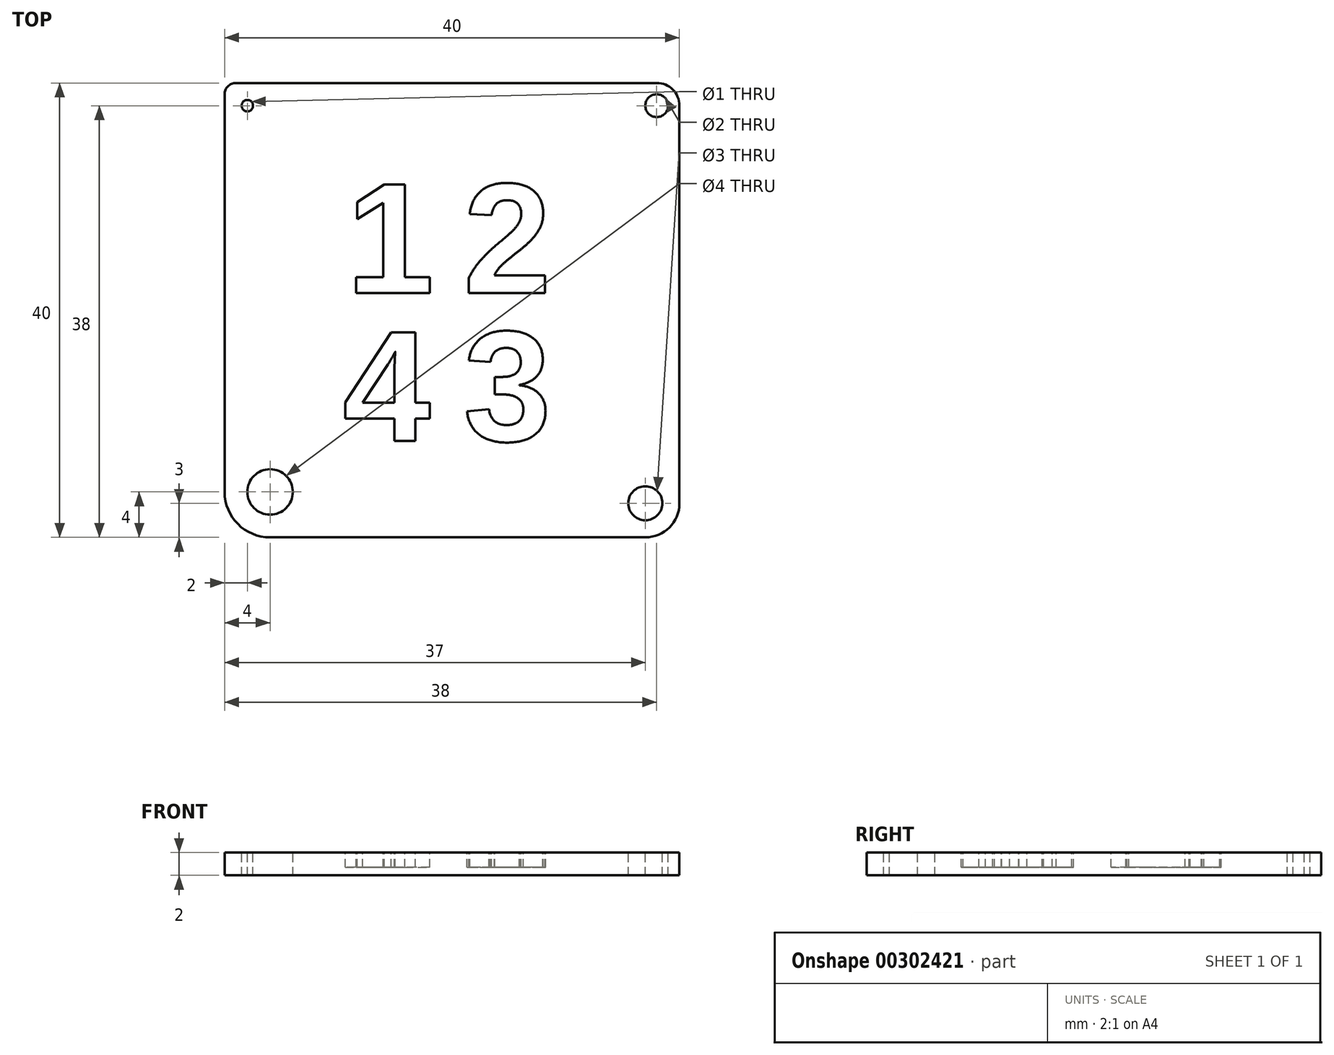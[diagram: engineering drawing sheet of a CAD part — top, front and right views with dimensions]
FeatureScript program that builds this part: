
annotation { "Feature Type Name" : "Feature", "Feature Type Description" : "" }
export const myFeature = defineFeature(function(context is Context, id is Id, definition is map)
    precondition{}
    {
        {
            var Q0;
            Q0=qCreatedBy(makeId("Top.planeOp"),FACE);
            var sketch = newSketch(context, id + "F0", { "sketchPlane" : qUnion([Q0])});
            skLineSegment(sketch, "E0.bottom", {"start": v(-19, 20) * mm, "end": v(18, 20) * mm});
            skLineSegment(sketch, "E0.top", {"start": v(-16, -20) * mm, "end": v(17, -20) * mm});
            skLineSegment(sketch, "E0.left", {"start": v(-20, 19) * mm, "end": v(-20, -16) * mm});
            skLineSegment(sketch, "E0.right", {"start": v(20, 18) * mm, "end": v(20, -17) * mm});
            skPoint(sketch, "E0.middle", {"position": v(0, 0) * mm});
            skPoint(sketch, "E1.visualSharp", {"position": v(-20, 20) * mm});
            skArc(sketch, "E1.filletArc", {"start": v(-19, 20) * mm, "mid": v(-19.7, 19.7) * mm, "end": v(-20, 19) * mm});
            skPoint(sketch, "E2.visualSharp", {"position": v(20, 20) * mm});
            skArc(sketch, "E2.filletArc", {"start": v(20, 18) * mm, "mid": v(19.41, 19.41) * mm, "end": v(18, 20) * mm});
            skPoint(sketch, "E3.visualSharp", {"position": v(20, -20) * mm});
            skArc(sketch, "E3.filletArc", {"start": v(17, -20) * mm, "mid": v(19.12, -19.12) * mm, "end": v(20, -17) * mm});
            skPoint(sketch, "E4.visualSharp", {"position": v(-20, -20) * mm});
            skArc(sketch, "E4.filletArc", {"start": v(-20, -16) * mm, "mid": v(-18.83, -18.83) * mm, "end": v(-16, -20) * mm});
            skSolve(sketch);
        }
        {
            var Q0;
            Q0=makeQuery(id+"F0.imprint","IMPRINT",FACE,{"disambiguationData":[TD([[makeQuery(id+"F0.imprint","IMPRINT",EDGE,{"derivedFrom":sQuery(id+"F0.wireOp",EDGE,"E0.bottom")}),-1.0]])]});
            extrude(context, id + "F1", {"entities" : qUnion([Q0]), "depth" : 2 * mm});
        }
        {
            var Q0;
            Q0=makeQuery(id+"F1.opExtrude","CAP_FACE",FACE,{"disambiguationData":[OSD([sQuery(id+"F0.wireOp",EDGE,"E0.bottom"),sQuery(id+"F0.wireOp",EDGE,"E0.top"),sQuery(id+"F0.wireOp",EDGE,"E0.left"),sQuery(id+"F0.wireOp",EDGE,"E0.right"),sQuery(id+"F0.wireOp",EDGE,"E1.filletArc"),sQuery(id+"F0.wireOp",EDGE,"E2.filletArc"),sQuery(id+"F0.wireOp",EDGE,"E3.filletArc"),sQuery(id+"F0.wireOp",EDGE,"E4.filletArc")])],"isStart":false});
            var sketch = newSketch(context, id + "F2", { "sketchPlane" : qUnion([Q0])});
            skLineSegment(sketch, "E5.bottom", {"start": v(-1, -1.5) * mm, "end": v(1, -1.5) * mm});
            skLineSegment(sketch, "E5.top", {"start": v(-1, 1.5) * mm, "end": v(1, 1.5) * mm});
            skLineSegment(sketch, "E5.left", {"start": v(-1, -1.5) * mm, "end": v(-1, 1.5) * mm});
            skLineSegment(sketch, "E5.right", {"start": v(1, -1.5) * mm, "end": v(1, 1.5) * mm});
            skPoint(sketch, "E5.middle", {"position": v(0, 0) * mm});
            skPoint(sketch, "E6", {"position": v(-1, 1.5) * mm});
            skText(sketch, "E7", { "text": "1", "fontName": "Arimo-Bold.ttf"});
            skText(sketch, "E8", { "text": "2", "fontName": "Arimo-Bold.ttf"});
            skText(sketch, "E9", { "text": "4", "fontName": "Arimo-Bold.ttf"});
            skText(sketch, "E10", { "text": "3", "fontName": "Arimo-Bold.ttf"});
            skCircle(sketch, "E11", {"center": v(-16, -16) * mm, "radius": 2 * mm});
            skCircle(sketch, "E12", {"center": v(-18, 18) * mm, "radius": 0.5 * mm});
            skCircle(sketch, "E13", {"center": v(18, 18) * mm, "radius": 1 * mm});
            skCircle(sketch, "E14", {"center": v(17, -17) * mm, "radius": 1.5 * mm});
            const initialGuessF2  = {"E7": [-0.0093, 0.0015, 1, 0, 0.01], "E8": [0.001, 0.0015, 1, 0, 0.01], "E9": [-0.00961, -0.0115, 1, 0, 0.01], "E10": [0.001, -0.0115, 1, 0, 0.01]};
            skSetInitialGuess(sketch, initialGuessF2);
            skSolve(sketch);
        }
        {
            var Q0;
            Q0=makeQuery(id+"F2.imprint","IMPRINT",FACE,{"disambiguationData":[TD([[makeQuery(id+"F2.imprint","IMPRINT",EDGE,{"derivedFrom":sQuery(id+"F2.wireOp",EDGE,"E12")}),1.0]])]});
            var Q1;
            Q1=makeQuery(id+"F2.imprint","IMPRINT",FACE,{"disambiguationData":[TD([[makeQuery(id+"F2.imprint","IMPRINT",EDGE,{"derivedFrom":sQuery(id+"F2.wireOp",EDGE,"E13")}),1.0]])]});
            var Q2;
            Q2=makeQuery(id+"F2.imprint","IMPRINT",FACE,{"disambiguationData":[TD([[makeQuery(id+"F2.imprint","IMPRINT",EDGE,{"derivedFrom":sQuery(id+"F2.wireOp",EDGE,"E14")}),1.0]])]});
            var Q3;
            Q3=makeQuery(id+"F2.imprint","IMPRINT",FACE,{"disambiguationData":[TD([[makeQuery(id+"F2.imprint","IMPRINT",EDGE,{"derivedFrom":sQuery(id+"F2.wireOp",EDGE,"E11")}),1.0]])]});
            var Q4;
            Q4=sQuery(id+"F2.wireOp",EDGE,"E12");
            var Q5;
            Q5=sQuery(id+"F2.wireOp",EDGE,"E13");
            var Q6;
            Q6=sQuery(id+"F2.wireOp",EDGE,"E14");
            var Q7;
            Q7=sQuery(id+"F2.wireOp",EDGE,"E11");
            extrude(context, id + "F3", {"entities" : qUnion([Q0, Q1, Q2, Q3]), "operationType" : NewBodyOperationType.REMOVE, "surfaceEntities" : qUnion([Q4, Q5, Q6, Q7]), "oppositeDirection" : true, "depth" : 25 * mm});
        }
        {
            var Q0;
            Q0=makeQuery(id+"F2.imprint","IMPRINT",FACE,{"disambiguationData":[TD([[makeQuery(id+"F2.imprint","IMPRINT",EDGE,{"derivedFrom":sQuery(id+"F2.wireOp",EDGE,"E7.sketch_text.stroke-0")}),-1.0]])]});
            var Q1;
            Q1=makeQuery(id+"F2.imprint","IMPRINT",FACE,{"disambiguationData":[TD([[makeQuery(id+"F2.imprint","IMPRINT",EDGE,{"derivedFrom":sQuery(id+"F2.wireOp",EDGE,"E8.sketch_text.stroke-0")}),-1.0]])]});
            var Q2;
            Q2=makeQuery(id+"F2.imprint","IMPRINT",FACE,{"disambiguationData":[TD([[makeQuery(id+"F2.imprint","IMPRINT",EDGE,{"derivedFrom":sQuery(id+"F2.wireOp",EDGE,"E10.sketch_text.stroke-0")}),-1.0]])]});
            var Q3;
            Q3=makeQuery(id+"F2.imprint","IMPRINT",FACE,{"disambiguationData":[TD([[makeQuery(id+"F2.imprint","IMPRINT",EDGE,{"derivedFrom":sQuery(id+"F2.wireOp",EDGE,"E9.sketch_text.stroke-0")}),-1.0]])]});
            extrude(context, id + "F4", {"entities" : qUnion([Q0, Q1, Q2, Q3]), "operationType" : NewBodyOperationType.REMOVE, "oppositeDirection" : true, "depth" : 1.3 * mm});
        }
    });
